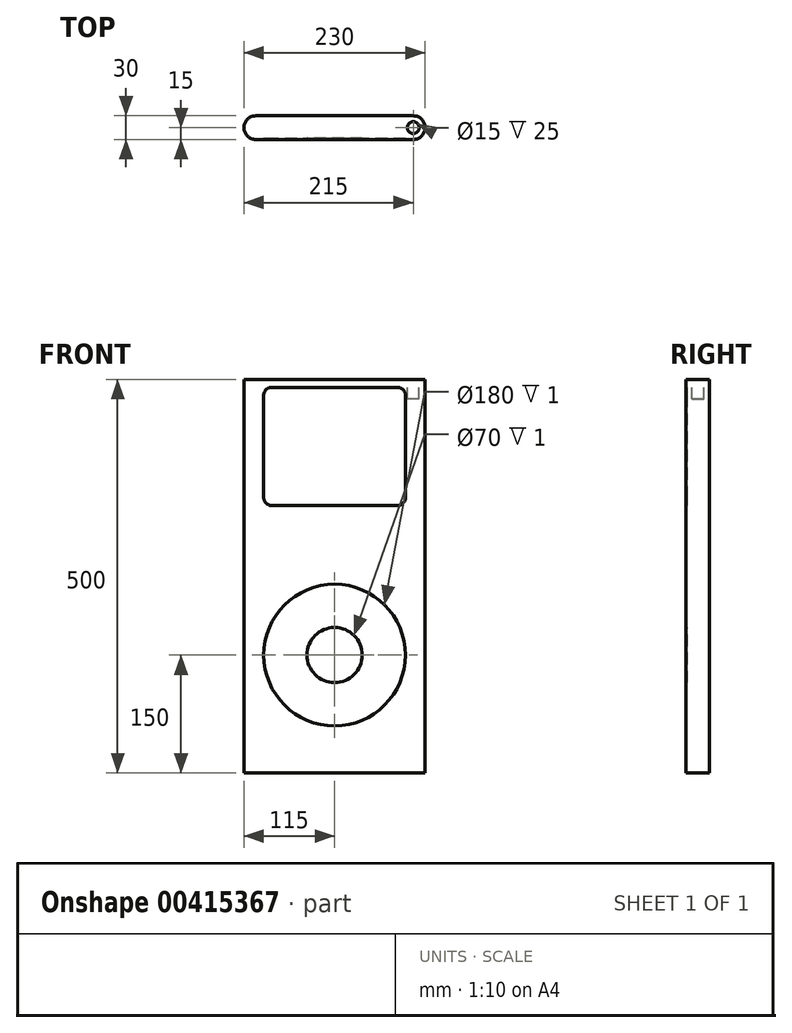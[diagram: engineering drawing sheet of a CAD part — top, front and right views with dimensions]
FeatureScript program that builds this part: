
annotation { "Feature Type Name" : "Feature", "Feature Type Description" : "" }
export const myFeature = defineFeature(function(context is Context, id is Id, definition is map)
    precondition{}
    {
        {
            var Q0;
            Q0=qCreatedBy(makeId("Top.planeOp"),FACE);
            var sketch = newSketch(context, id + "F0", { "sketchPlane" : qUnion([Q0])});
            skArc(sketch, "E0", {"start": v(0, 15) * mm, "mid": v(-15, 0) * mm, "end": v(0, -15) * mm});
            skArc(sketch, "E1", {"start": v(200, -15) * mm, "mid": v(215, 0) * mm, "end": v(200, 15) * mm});
            skLineSegment(sketch, "E2", {"start": v(0, 15) * mm, "end": v(200, 15) * mm});
            skLineSegment(sketch, "E3", {"start": v(200, 15) * mm, "end": v(0, 15) * mm});
            skLineSegment(sketch, "E4", {"start": v(0, -15) * mm, "end": v(200, -15) * mm});
            skSolve(sketch);
        }
        {
            var Q0;
            Q0 = qSketchRegion(id + "F0", true);
            extrude(context, id + "F1", {"entities" : qUnion([Q0]), "depth" : 500 * mm});
        }
        {
            var Q0;
            Q0=makeQuery(id+"F1.opExtrude","SWEPT_FACE",FACE,{"disambiguationData":[OSD([sQuery(id+"F0.wireOp",EDGE,"E4")])]});
            var sketch = newSketch(context, id + "F2", { "sketchPlane" : qUnion([Q0])});
            skLineSegment(sketch, "E5.bottom", {"start": v(20, 490) * mm, "end": v(180, 490) * mm});
            skLineSegment(sketch, "E5.top", {"start": v(20, 340) * mm, "end": v(180, 340) * mm});
            skLineSegment(sketch, "E5.left", {"start": v(10, 480) * mm, "end": v(10, 350) * mm});
            skLineSegment(sketch, "E5.right", {"start": v(190, 480) * mm, "end": v(190, 350) * mm});
            skPoint(sketch, "E6.visualSharp", {"position": v(10, 490) * mm});
            skArc(sketch, "E6.filletArc", {"start": v(20, 490) * mm, "mid": v(12.93, 487.07) * mm, "end": v(10, 480) * mm});
            skPoint(sketch, "E7.visualSharp", {"position": v(190, 490) * mm});
            skArc(sketch, "E7.filletArc", {"start": v(190, 480) * mm, "mid": v(187.07, 487.07) * mm, "end": v(180, 490) * mm});
            skPoint(sketch, "E8.visualSharp", {"position": v(10, 340) * mm});
            skArc(sketch, "E8.filletArc", {"start": v(10, 350) * mm, "mid": v(12.93, 342.93) * mm, "end": v(20, 340) * mm});
            skPoint(sketch, "E9.visualSharp", {"position": v(190, 340) * mm});
            skArc(sketch, "E9.filletArc", {"start": v(180, 340) * mm, "mid": v(187.07, 342.93) * mm, "end": v(190, 350) * mm});
            skSolve(sketch);
        }
        {
            var Q0;
            Q0 = qSketchRegion(id + "F2", true);
            extrude(context, id + "F3", {"entities" : qUnion([Q0]), "operationType" : NewBodyOperationType.REMOVE, "oppositeDirection" : true, "depth" : 1 * mm});
        }
        {
            var Q0;
            Q0=makeQuery(id+"F1.opExtrude","SWEPT_FACE",FACE,{"disambiguationData":[OSD([sQuery(id+"F0.wireOp",EDGE,"E4")])]});
            var sketch = newSketch(context, id + "F4", { "sketchPlane" : qUnion([Q0])});
            skCircle(sketch, "E10", {"center": v(100, 150) * mm, "radius": 90 * mm});
            skLineSegment(sketch, "E11", {"start": v(100, 0) * mm, "end": v(100, 150) * mm, "construction": true});
            skSolve(sketch);
        }
        {
            var Q0;
            Q0 = qSketchRegion(id + "F4", true);
            extrude(context, id + "F5", {"entities" : qUnion([Q0]), "operationType" : NewBodyOperationType.REMOVE, "oppositeDirection" : true, "depth" : 1 * mm});
        }
        {
            var Q0;
            Q0=makeQuery(id+"F5.boolean.opBoolean","COPY",FACE,{"derivedFrom":makeQuery(id+"F5.opExtrude","CAP_FACE",FACE,{"disambiguationData":[OSD([sQuery(id+"F4.wireOp",EDGE,"E10")])],"isStart":false})});
            var sketch = newSketch(context, id + "F6", { "sketchPlane" : qUnion([Q0])});
            skCircle(sketch, "E12", {"center": v(100, 150) * mm, "radius": 35 * mm});
            skSolve(sketch);
        }
        {
            var Q0;
            Q0 = qSketchRegion(id + "F6", true);
            extrude(context, id + "F7", {"entities" : qUnion([Q0]), "operationType" : NewBodyOperationType.REMOVE, "oppositeDirection" : true, "depth" : 1 * mm});
        }
        {
            var Q0;
            Q0=makeQuery(id+"F1.opExtrude","CAP_FACE",FACE,{"disambiguationData":[OSD([sQuery(id+"F0.wireOp",EDGE,"E0"),sQuery(id+"F0.wireOp",EDGE,"E1"),sQuery(id+"F0.wireOp",EDGE,"E3"),sQuery(id+"F0.wireOp",EDGE,"E4")])],"isStart":false});
            var sketch = newSketch(context, id + "F8", { "sketchPlane" : qUnion([Q0])});
            skCircle(sketch, "E13", {"center": v(200, 0) * mm, "radius": 7.5 * mm});
            skSolve(sketch);
        }
        {
            var Q0;
            Q0 = qSketchRegion(id + "F8", true);
            extrude(context, id + "F9", {"entities" : qUnion([Q0]), "operationType" : NewBodyOperationType.REMOVE, "oppositeDirection" : true, "depth" : 25 * mm});
        }
    });
